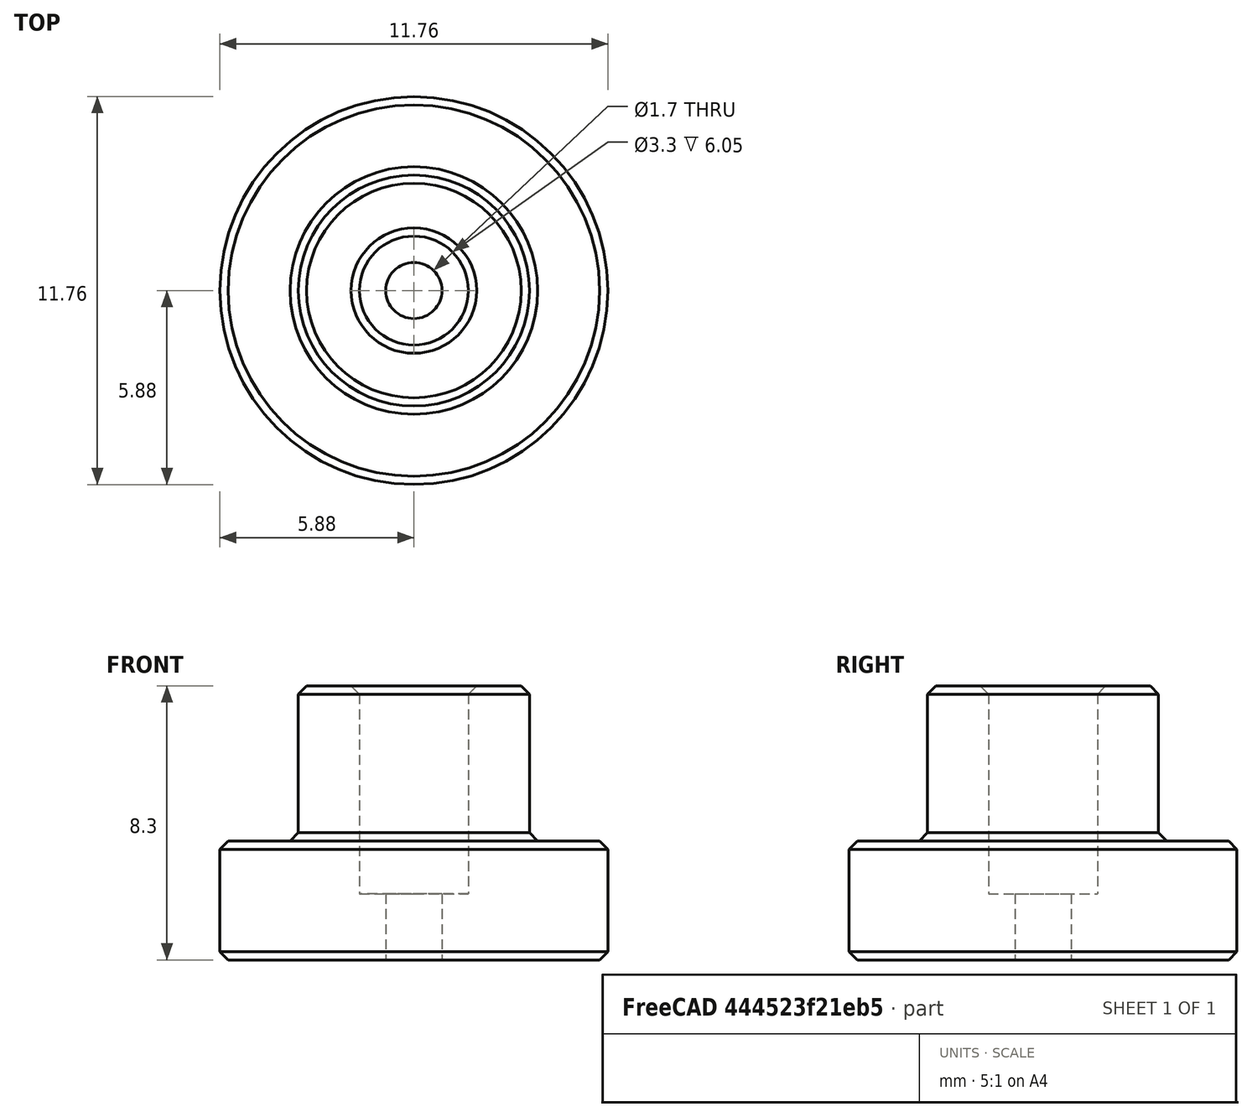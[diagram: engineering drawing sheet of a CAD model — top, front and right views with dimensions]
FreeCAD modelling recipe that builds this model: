
FCSTD DOCUMENT  (FreeCAD 1.0R38641 +678 (Git))
Label: SPACER
License: All rights reserved
LicenseURL: https://en.wikipedia.org/wiki/All_rights_reserved
objects: TechDraw::DrawViewDimension×7, Sketcher::SketchObject×2, TechDraw::DrawProjGroupItem×2, PartDesign::CoordinateSystem×2, TechDraw::DrawSVGTemplate×1, PartDesign::Revolution×1, TechDraw::DrawViewSection×1, TechDraw::DrawProjGroup×1, TechDraw::DrawViewBalloon×1, TechDraw::DrawPage×1, PartDesign::Body×1
note: 23 computed .brp shape members not serialized (recipe doc carries the construction recipe); baked Part::Feature solids carry a one-line shape summary decoded from their .brp

FEATURE [TechDraw::DrawSVGTemplate] Template
  EditableTexts = CreationDate=2026/03/20; E.G.APPROVED=Approved; FC-Scale=5:1; FC-Title=SPACER; IntechStudioLtd.=Intech Studio Ltd.; MATERIAL=brass; REV=04; STANDARD=+/-0,1
  Height = 297
  Orientation = 1
  Template = <userpath>/Documents/grid-hardware/Manufacturing/FreeCAD_technical_drawing_template/A3_LandscapeTD_MODIFIED.svg
  Width = 420
FEATURE [Sketcher::SketchObject] Sketch009
  ArcFitTolerance = 0
  AttachmentSupport = -> [YZ_Plane004]
  FullyConstrained = true
  MakeInternals = false
  MapMode = 5
  Placement = pos=(0,0,0) rot=(0.57735,0.57735,0.57735;2.0944rad)
  sketch-geometry (1):
    g0: LineSegment StartX=0 StartY=9 StartZ=0 EndX=0 EndY=-1 EndZ=0
  constraints (4):
    c: PointOnObject(g0,g-2)
    c: DistanceY(g0,g0) = 10
    c: DistanceY(g0,g-1) = 1
    c: Vertical(g0)
FEATURE [Sketcher::SketchObject] Sketch008
  ArcFitTolerance = 0
  AttachmentSupport = -> [YZ_Plane004]
  FullyConstrained = true
  MakeInternals = false
  MapMode = 5
  Placement = pos=(0,0,0) rot=(0.57735,0.57735,0.57735;2.0944rad)
  expr: Constraints[16] = 3.3 / 2
  expr: Constraints[24] = 5.875 mm
  sketch-geometry (23):
    g0: LineSegment StartX=-1.9 StartY=8.3 StartZ=0 EndX=-3.25 EndY=8.3 EndZ=0
    g1: LineSegment StartX=-1.65 StartY=8.05 StartZ=0 EndX=-1.65 EndY=2 EndZ=0
    g2: LineSegment StartX=-1.65 StartY=2 StartZ=0 EndX=-0.85 EndY=2 EndZ=0
    g3: LineSegment StartX=-0.85 StartY=2 StartZ=0 EndX=-0.85 EndY=0 EndZ=0
    g4: LineSegment StartX=-0.85 StartY=0 StartZ=0 EndX=-5.625 EndY=0 EndZ=0
    g5: LineSegment StartX=-5.625 StartY=0 StartZ=0 EndX=-5.875 EndY=0.25 EndZ=0
    g6: LineSegment StartX=-3.5 StartY=8.05 StartZ=0 EndX=-3.25 EndY=8.3 EndZ=0
    g7: LineSegment StartX=-1.9 StartY=8.3 StartZ=0 EndX=-1.65 EndY=8.05 EndZ=0
    g8: LineSegment StartX=-5.875 StartY=3.35 StartZ=0 EndX=-5.875 EndY=0.25 EndZ=0
    g9: LineSegment StartX=-5.625 StartY=3.6 StartZ=0 EndX=-5.875 EndY=3.35 EndZ=0
    g10: LineSegment StartX=-3.75 StartY=3.6 StartZ=0 EndX=-5.625 EndY=3.6 EndZ=0
    g11: LineSegment StartX=-3.5 StartY=8.05 StartZ=0 EndX=-3.5 EndY=3.85 EndZ=0
    g12: LineSegment StartX=-3.5 StartY=3.85 StartZ=0 EndX=-3.75 EndY=3.6 EndZ=0
    g13: LineSegment [constr] StartX=-3.5 StartY=8.05 StartZ=0 EndX=-3.25 EndY=8.05 EndZ=0
    g14: LineSegment [constr] StartX=-3.25 StartY=8.05 StartZ=0 EndX=-3.25 EndY=8.3 EndZ=0
    g15: LineSegment [constr] StartX=-1.9 StartY=8.3 StartZ=0 EndX=-1.9 EndY=8.05 EndZ=0
    g16: LineSegment [constr] StartX=-1.9 StartY=8.05 StartZ=0 EndX=-1.65 EndY=8.05 EndZ=0
    g17: LineSegment [constr] StartX=-3.75 StartY=3.6 StartZ=0 EndX=-3.5 EndY=3.6 EndZ=0
    g18: LineSegment [constr] StartX=-3.5 StartY=3.6 StartZ=0 EndX=-3.5 EndY=3.85 EndZ=0
    g19: LineSegment [constr] StartX=-5.875 StartY=3.35 StartZ=0 EndX=-5.625 EndY=3.35 EndZ=0
    g20: LineSegment [constr] StartX=-5.625 StartY=3.35 StartZ=0 EndX=-5.625 EndY=3.6 EndZ=0
    g21: LineSegment [constr] StartX=-5.875 StartY=0.25 StartZ=0 EndX=-5.625 EndY=0.25 EndZ=0
    g22: LineSegment [constr] StartX=-5.625 StartY=0.25 StartZ=0 EndX=-5.625 EndY=0 EndZ=0
  constraints (65):
    c: Horizontal(g0)
    c: Coincident(g2,g1)
    c: Horizontal(g2)
    c: Vertical(g1)
    c: Vertical(g3)
    c: Coincident(g2,g3)
    c: DistanceX(g2,g-1) = 0.85
    c: Horizontal(g4)
    c: Coincident(g11,g6)
    c: Coincident(g0,g6)
    c: DistanceY(g11,g0) = 0.25
    c: Coincident(g8,g5)
    c: Coincident(g4,g5)
    c: Angle(g7,g1) = 2.35619
    c: Coincident(g0,g7)
    c: Coincident(g1,g7)
    c: DistanceX(g1,g-1) = 1.65
    c: DistanceY(g-1,g3) = 0
    c: DistanceY(g-1,g2) = 2
    c: DistanceY(g-1,g4) = 0
    c: DistanceY(g-1,g0) = 8.3
    c: Equal(g5,g6)
    c: Equal(g7,g6)
    c: Coincident(g4,g3)
    c: DistanceX(g8,g-1) = 5.875
    c: Coincident(g9,g8)
    c: Vertical(g8)
    c: Coincident(g10,g9)
    c: Coincident(g12,g10)
    c: Coincident(g11,g12)
    c: Vertical(g11)
    c: Horizontal(g10)
    c: Coincident(g6,g13)
    c: Horizontal(g13)
    c: Coincident(g13,g14)
    c: Coincident(g14,g0)
    c: Coincident(g0,g15)
    c: Vertical(g15)
    c: Coincident(g15,g16)
    c: Coincident(g16,g1)
    c: Horizontal(g16)
    c: Vertical(g14)
    c: Equal(g13,g14)
    c: Coincident(g10,g17)
    c: Horizontal(g17)
    c: Coincident(g17,g18)
    c: Coincident(g18,g11)
    c: Vertical(g18)
    c: Coincident(g8,g19)
    c: Horizontal(g19)
    c: Coincident(g19,g20)
    c: Coincident(g20,g9)
    c: Vertical(g20)
    c: Equal(g20,g19)
    c: Equal(g17,g18)
    c: Equal(g12,g9)
    c: Equal(g9,g5)
    c: Coincident(g5,g21)
    c: Coincident(g21,g22)
    c: Coincident(g22,g4)
    c: Vertical(g22)
    c: Horizontal(g21)
    c: Equal(g21,g22)
    c: DistanceY(g4,g9) = 3.6
    c: DistanceX(g11,g-1) = 3.5
FEATURE [PartDesign::Revolution] Revolution
  Angle = 360
  Angle2 = 60
  Axis = (0,0,1)
  Base = (0,0,0)
  Placement = pos=(0,0,0) rot=(1,1,1;2.0944rad)
  Profile = -> Sketch008
  ReferenceAxis = -> Sketch008 [V_Axis]
  Suppressed = false
  Type = 0
FEATURE [TechDraw::DrawProjGroupItem] ProjItem  label="Front"
  CoarseView = false
  Direction = (0,-1,0)
  Focus = 100
  HardHidden = false
  IsoCount = 0
  IsoHidden = false
  IsoVisible = false
  LockPosition = true
  Perspective = false
  Rotation = 0
  RotationVector = (1,0,0)
  Scale = 5
  ScaleType = 2
  ScrubCount = 0
  SeamHidden = false
  SeamVisible = false
  SmoothHidden = false
  SmoothVisible = true
  Source = -> [Revolution]
  Type = 0
  X = 0
  XDirection = (1,0,0)
  Y = 0
FEATURE [TechDraw::DrawViewSection] SectionView  label="Section A - A"
  BaseView = -> ProjItem
  Caption = Section A - A
  CoarseView = false
  CutSurfaceDisplay = 2
  Direction = (-1,0,-1e-16)
  FileGeomPattern = /snap/freecad/1202/usr/share/Mod/TechDraw/PAT/FCPAT.pat
  FileHatchPattern = /snap/freecad/1202/usr/share/Mod/TechDraw/Patterns/simple.svg
  Focus = 100
  FuseBeforeCut = false
  HardHidden = false
  HatchOffset = (0,0,0)
  HatchRotation = 0
  HatchScale = 1
  IsoCount = 0
  IsoHidden = false
  IsoVisible = false
  LockPosition = false
  NameGeomPattern = Diamond
  Perspective = false
  Rotation = -90
  Scale = 5
  ScaleType = 0
  ScrubCount = 0
  SeamHidden = false
  SeamVisible = false
  SectionDirection = 4
  SectionLineStretch = 1
  SectionNormal = (-1,0,-1e-16)
  SectionOrigin = (0,0,4.15)
  SectionSymbol = A
  SmoothHidden = false
  SmoothVisible = true
  Source = -> [Revolution]
  TrimAfterCut = false
  UsePreviousCut = false
  X = 249.527
  XDirection = (1e-16,0,-1)
  Y = 208.158
FEATURE [TechDraw::DrawProjGroupItem] ProjItem001  label="Top"
  CoarseView = false
  Direction = (0,0,1)
  Focus = 100
  HardHidden = false
  IsoCount = 0
  IsoHidden = false
  IsoVisible = false
  LockPosition = false
  Perspective = false
  Rotation = 0
  RotationVector = (1,0,0)
  ScaleType = 2
  ScrubCount = 0
  SeamHidden = false
  SeamVisible = false
  SmoothHidden = false
  SmoothVisible = true
  Source = -> [Revolution]
  Type = 4
  X = 0
  XDirection = (1,0,0)
  Y = -90.125
FEATURE [TechDraw::DrawProjGroup] ProjGroup
  Anchor = -> ProjItem
  AutoDistribute = true
  LockPosition = false
  ProjectionType = 0
  Rotation = 0
  Scale = 5
  ScaleType = 0
  Source = -> [Revolution]
  Views = -> [ProjItem,ProjItem001]
  X = 106.303
  Y = 208.166
  spacingX = 40
  spacingY = 40
FEATURE [TechDraw::DrawViewBalloon] Balloon
  BubbleShape = 1
  EndType = 0
  EndTypeScale = 5
  KinkLength = 5
  LockPosition = false
  OriginX = 4
  OriginY = 4.4
  Rotation = 0
  Scale = 5
  ScaleType = 0
  ShapeScale = 1
  SourceView = -> ProjItem
  Text = Chamfer 0.25mm x 45°
  TextWrapLen = -1
  X = 13.3781
  Y = 6.53229
FEATURE [TechDraw::DrawViewDimension] Dimension002
  AngleOverride = false
  Arbitrary = false
  ArbitraryTolerances = false
  BoxCorners = (2) [(-29.375,-20.75,-1e-07),(29.375,20.75,1e-07)]
  EqualTolerance = true
  ExtensionAngle = 0
  FormatSpec = ⌀%.2w
  FormatSpecOverTolerance = %+.2w
  FormatSpecUnderTolerance = %+.2w
  Inverted = false
  LineAngle = 0
  LockPosition = false
  MeasureType = 1
  OverTolerance = 0
  References2D = -> [SectionView]
  Rotation = 0
  Scale = 5
  ScaleType = 0
  TheoreticalExact = false
  Type = 1
  UnderTolerance = 0
  X = 0
  Y = 35.4315
FEATURE [TechDraw::DrawViewDimension] Dimension003
  AngleOverride = false
  Arbitrary = false
  ArbitraryTolerances = false
  BoxCorners = (2) [(-29.375,-20.75,-1e-07),(29.375,20.75,1e-07)]
  EqualTolerance = false
  ExtensionAngle = 0
  FormatSpec = ⌀%.2w
  FormatSpecOverTolerance = %+.2w
  FormatSpecUnderTolerance = %+.2w
  Inverted = false
  LineAngle = 0
  LockPosition = false
  MeasureType = 1
  OverTolerance = 0.2
  References2D = -> [SectionView]
  Rotation = 0
  Scale = 5
  ScaleType = 0
  TheoreticalExact = false
  Type = 1
  UnderTolerance = 0
  X = 0
  Y = 52.7979
FEATURE [TechDraw::DrawViewDimension] Dimension004
  AngleOverride = false
  Arbitrary = false
  ArbitraryTolerances = false
  BoxCorners = (2) [(-29.375,-20.75,-1e-07),(29.375,20.75,1e-07)]
  EqualTolerance = true
  ExtensionAngle = 0
  FormatSpec = %.2w
  FormatSpecOverTolerance = %+.2w
  FormatSpecUnderTolerance = %+.2w
  Inverted = false
  LineAngle = 0
  LockPosition = false
  MeasureType = 1
  OverTolerance = 0
  References2D = -> [SectionView]
  Rotation = 0
  Scale = 5
  ScaleType = 0
  TheoreticalExact = false
  Type = 2
  UnderTolerance = 0
  X = -49.6071
  Y = -15.75
FEATURE [TechDraw::DrawViewDimension] Dimension005
  AngleOverride = false
  Arbitrary = false
  ArbitraryTolerances = false
  BoxCorners = (2) [(-29.375,-20.75,-1e-07),(29.375,20.75,1e-07)]
  EqualTolerance = true
  ExtensionAngle = 0
  FormatSpec = ⌀%.2w
  FormatSpecOverTolerance = %+.2w
  FormatSpecUnderTolerance = %+.2w
  Inverted = false
  LineAngle = 0
  LockPosition = false
  MeasureType = 1
  OverTolerance = 0
  References2D = -> [SectionView]
  Rotation = 0
  Scale = 5
  ScaleType = 0
  TheoreticalExact = false
  Type = 1
  UnderTolerance = 0
  X = 0
  Y = 71.5638
FEATURE [TechDraw::DrawViewDimension] Dimension
  AngleOverride = false
  Arbitrary = false
  ArbitraryTolerances = false
  BoxCorners = (2) [(-29.375,-29.375,0),(29.375,29.375,0)]
  EqualTolerance = true
  ExtensionAngle = 0
  FormatSpec = ⌀%.2w
  FormatSpecOverTolerance = %+.2w
  FormatSpecUnderTolerance = %+.2w
  Inverted = false
  LineAngle = 0
  LockPosition = false
  MeasureType = 1
  OverTolerance = 0
  References2D = -> [ProjItem001]
  Rotation = 0
  Scale = 5
  ScaleType = 0
  TheoreticalExact = false
  Type = 5
  UnderTolerance = 0
  X = -60.0722
  Y = -17.5385
FEATURE [TechDraw::DrawViewDimension] Dimension006
  AngleOverride = false
  Arbitrary = false
  ArbitraryTolerances = false
  BoxCorners = (2) [(-29.375,-20.75,-1e-07),(29.375,20.75,1e-07)]
  EqualTolerance = false
  ExtensionAngle = 0
  FormatSpec = %.2w
  FormatSpecOverTolerance = %+.2w
  FormatSpecUnderTolerance = %+.2w
  Inverted = false
  LineAngle = 0
  LockPosition = false
  MeasureType = 1
  OverTolerance = 0
  References2D = -> [ProjItem]
  Rotation = 0
  Scale = 5
  ScaleType = 0
  TheoreticalExact = false
  Type = 0
  UnderTolerance = -0.1
  X = -58.7208
  Y = -36.3695
FEATURE [TechDraw::DrawViewDimension] Dimension007
  AngleOverride = false
  Arbitrary = false
  ArbitraryTolerances = false
  BoxCorners = (2) [(-29.375,-20.75,-1e-07),(29.375,20.75,1e-07)]
  EqualTolerance = false
  ExtensionAngle = 0
  FormatSpec = %.2w
  FormatSpecOverTolerance = %+.2w
  FormatSpecUnderTolerance = %+.2w
  Inverted = false
  LineAngle = 0
  LockPosition = false
  MeasureType = 1
  OverTolerance = 0
  References2D = -> [ProjItem]
  Rotation = 0
  Scale = 5
  ScaleType = 0
  TheoreticalExact = false
  Type = 0
  UnderTolerance = -0.1
  X = -39.8312
  Y = -37.1705
FEATURE [TechDraw::DrawPage] Page  label="SPACER_Drawing"
  KeepUpdated = true
  NextBalloonIndex = 2
  ProjectionType = 0
  Scale = 5
  Template = -> Template
  Views = -> [SectionView,ProjGroup,Balloon,Dimension002,Dimension003,Dimension004,Dimension005,Dimension,Dimension006,Dimension007]
FEATURE [PartDesign::CoordinateSystem] LCS_1
  AttacherType = Attacher::AttachEngine3D
FEATURE [PartDesign::CoordinateSystem] LCS_2
  AttacherType = Attacher::AttachEngine3D
  AttachmentSupport = -> [Revolution]
  MapMode = 11
  Placement = pos=(-7e-16,2e-16,2) rot=(0,0,1;0rad)
FEATURE [PartDesign::Body] Body004  label="SPACER"
  AllowCompound = false
  Group = -> [Sketch008,Revolution,Sketch009,LCS_1,LCS_2]
  Origin = -> Origin004
  Tip = -> Revolution
